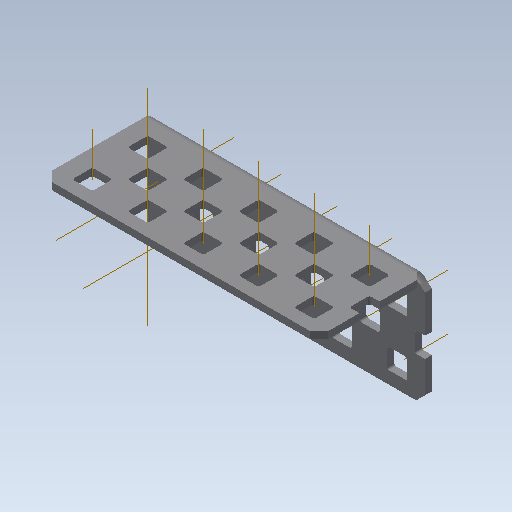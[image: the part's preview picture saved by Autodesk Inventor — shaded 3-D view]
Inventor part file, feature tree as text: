
AUTODESK INVENTOR PART (.ipt)
format: ipt  version: 2020 (Build 240168000, 168)  size: 1,833,472 bytes
history: native  units: in
note: dims shown in document units (in); Inventor stores cm internally (conversion verified against a paired STEP export)
features: other x35, pattern_linear x4, sheet_metal_op x1, extrude x1, imported_body x1, sketch x1
ambient origin geometry x8: Origin, YZ Plane, XZ Plane, XY Plane, X Axis, Y Axis, Z Axis, Center Point
bodies: Body1 (feature_tree)
feature tree (43):
  sheet_metal_op  "Fold1"
  other  "L-Channel"
  extrude  "length cut"  Depth=0.5in
  other  "top out axis"
  other  "top inner axis"
  other  "back out axis"
  other  "back inner axis"
  pattern_linear  "top outer axes"  Count1=2 Spacing1=0.5in
  pattern_linear  "top inner axes"  Spacing1=0.5in  [1 undecoded]
  pattern_linear  "back outer axes"  Count1=2 Spacing1=0.5in
  pattern_linear  "back inner axes"  Spacing1=0.5in  [1 undecoded]
  other  "right plane"
  imported_body  "Base1"
  sketch  "Sketch1"  dims[d1=0.0in d4=0.5in d5=0.7874in d7=0.5in d10=0.5in d13=0.5in d14=0.7874in d16=0.5in d19=0.5in d20=-2.5in d21=0.0in d22=0.0in d23=0.0in d24=0.0in d25=0.0in d26=0.0in]
  other  "Work Point1"
  other  "Work Point2"
  other  "Work Point3"
  other  "Work Point4"
  other  "Work Axis5"
  other  "Work Axis6"
  other  "Work Axis7"
  other  "Work Axis8"
  other  "Work Axis11"
  other  "Work Axis12"
  other  "Work Axis13"
  other  "Work Axis14"
  other  "Work Axis15"
  other  "Work Axis18"
  other  "Work Axis19"
  other  "Work Axis20"
  other  "Work Axis23"
  other  "Work Axis24"
  other  "Work Axis25"
  other  "Work Axis26"
  other  "Work Axis29"
  other  "Work Axis30"
  other  "Work Axis31"
  other  "Work Axis32"
  other  "Work Axis33"
  other  "Work Axis36"
  other  "Work Axis37"
  other  "Work Axis38"
  other  "left plane"
note: 2 required parameter values undecoded (feature->parameter linkage not recoverable at this tier; creation-order binding heuristic only, values carry confidence <= 0.55)
